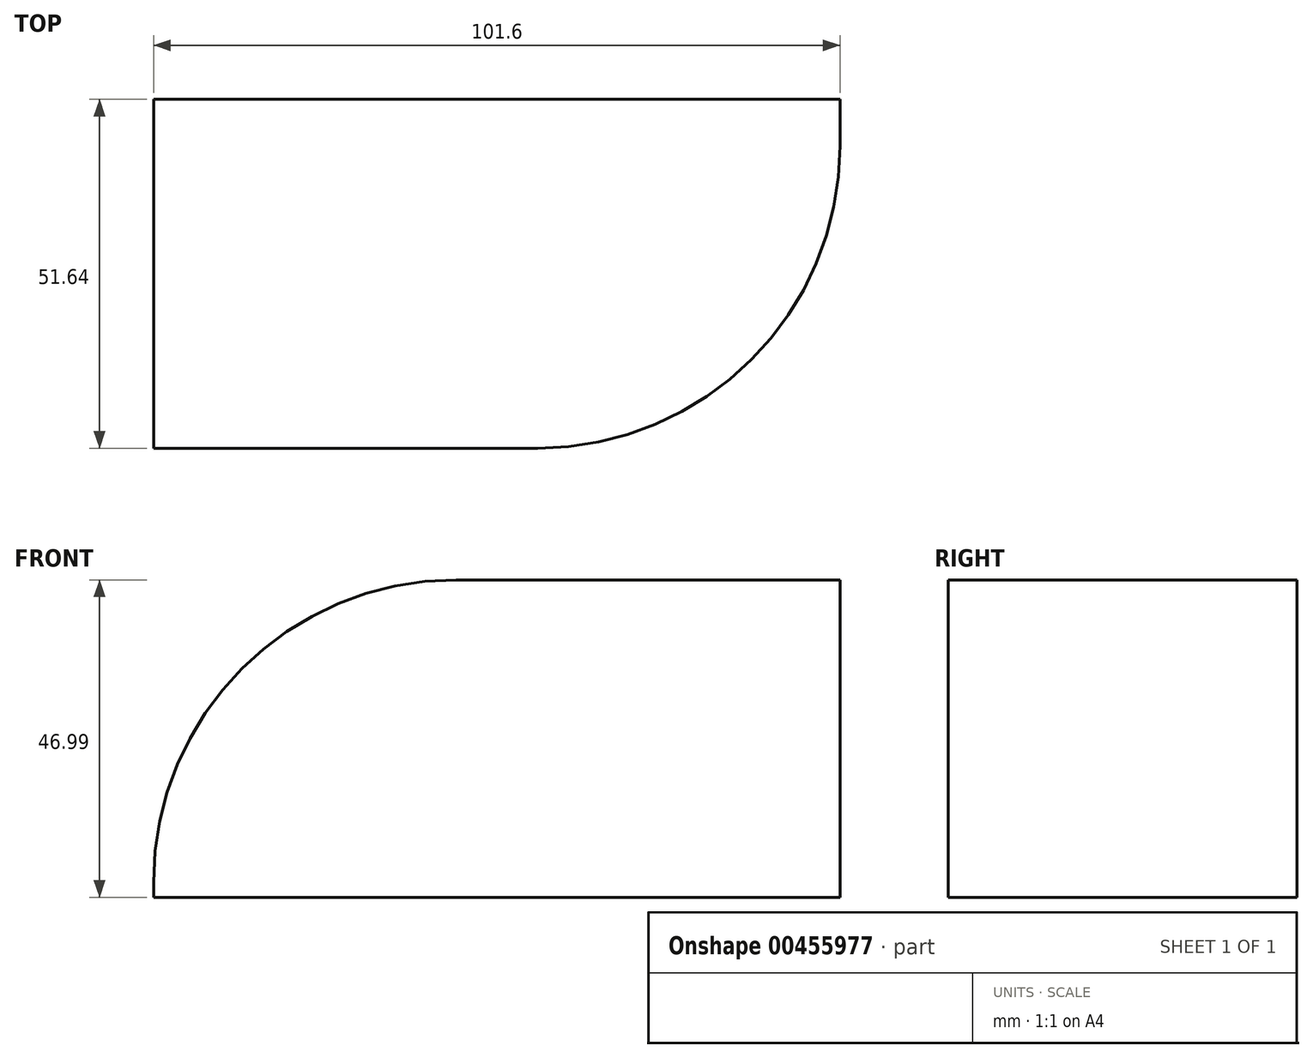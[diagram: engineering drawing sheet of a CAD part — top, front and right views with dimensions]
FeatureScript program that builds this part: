
annotation { "Feature Type Name" : "Feature", "Feature Type Description" : "" }
export const myFeature = defineFeature(function(context is Context, id is Id, definition is map)
    precondition{}
    {
        {
            var Q0;
            Q0=qCreatedBy(makeId("Top.planeOp"),FACE);
            var sketch = newSketch(context, id + "F0", { "sketchPlane" : qUnion([Q0])});
            skLineSegment(sketch, "E0.bottom", {"start": v(-50.8, 25.82) * mm, "end": v(50.8, 25.82) * mm});
            skLineSegment(sketch, "E0.top", {"start": v(-50.8, -25.82) * mm, "end": v(50.8, -25.82) * mm});
            skLineSegment(sketch, "E0.left", {"start": v(-50.8, 25.82) * mm, "end": v(-50.8, -25.82) * mm});
            skLineSegment(sketch, "E0.right", {"start": v(50.8, 25.82) * mm, "end": v(50.8, -25.82) * mm});
            skPoint(sketch, "E0.middle", {"position": v(0, 0) * mm});
            skSolve(sketch);
        }
        {
            var Q0;
            Q0 = qSketchRegion(id + "F0", true);
            extrude(context, id + "F1", {"entities" : qUnion([Q0]), "depth" : 47 * mm});
        }
        {
            var Q0;
            Q0=makeQuery(id+"F1.opExtrude","CAP_EDGE",EDGE,{"disambiguationData":[OSD([sQuery(id+"F0.wireOp",EDGE,"E0.left")])],"isStart":false});
            var Q1;
            Q1=makeQuery(id+"F1.opExtrude","SWEPT_EDGE",EDGE,{"disambiguationData":[OSD([sQuery(id+"F0.wireOp",EDGE,"E0.top"),sQuery(id+"F0.wireOp",EDGE,"E0.right")])]});
            fillet(context, id + "F2", {"entities" : qUnion([Q0, Q1]), "radius" : 44.76 * mm, "tangentPropagation" : true, "allowEdgeOverflow" : false});
        }
    });
